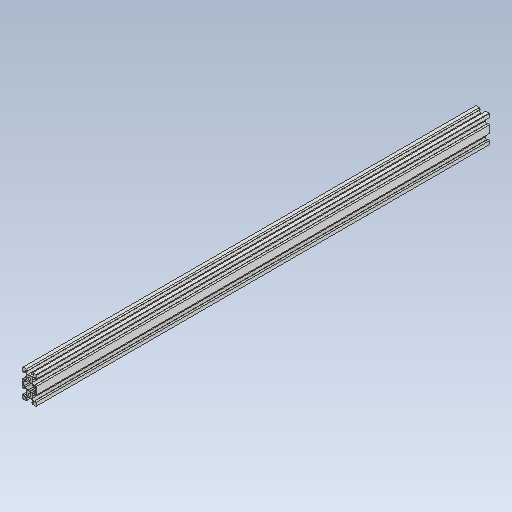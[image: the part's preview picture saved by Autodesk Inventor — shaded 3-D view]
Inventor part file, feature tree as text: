
AUTODESK INVENTOR PART (.ipt)
format: ipt  version: 2020 (Build 240168000, 168)  size: 219,648 bytes
history: native  units: mm
features: extrude x1, sketch x1
ambient origin geometry x8: Origin, YZ Plane, XZ Plane, XY Plane, X Axis, Y Axis, Z Axis, Center Point
bodies: Solid1 (feature_tree)
feature tree (2):
  extrude  "Extrusion1"  [1 undecoded]
  sketch  "Sketch1"  dims[d0=660.0mm d1=0.0mm]
note: 1 required parameter value undecoded (feature->parameter linkage not recoverable at this tier; creation-order binding heuristic only, values carry confidence <= 0.55)
